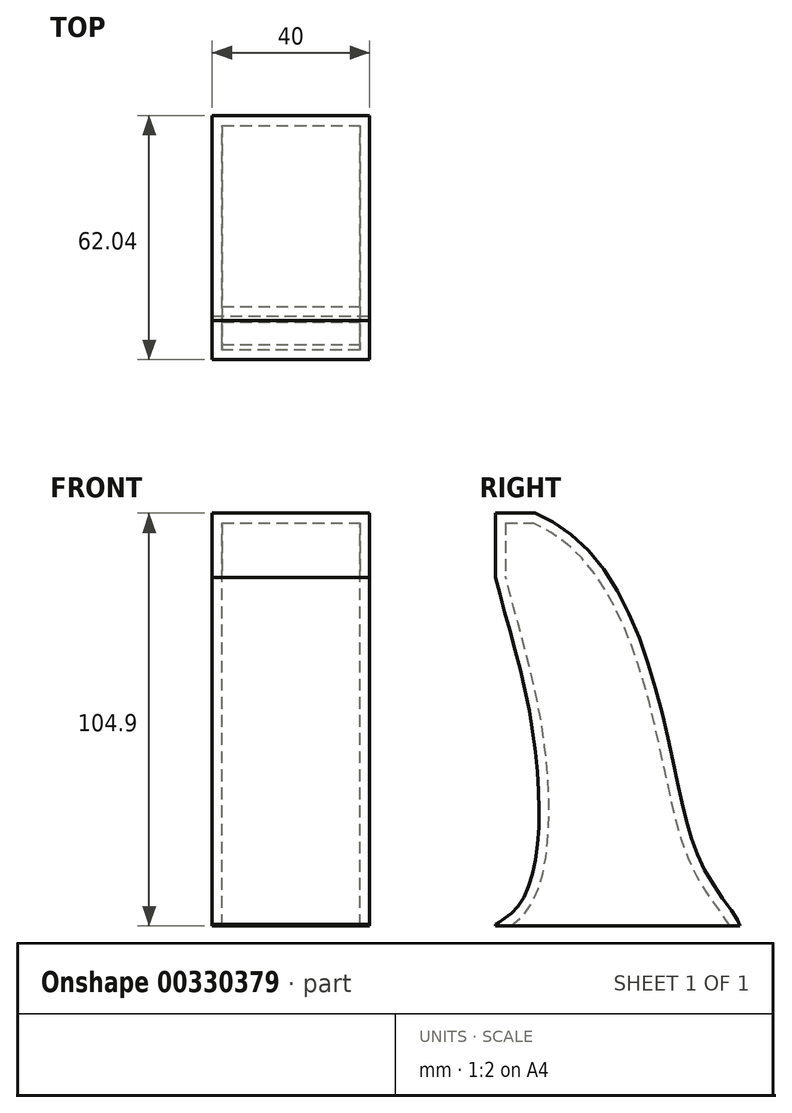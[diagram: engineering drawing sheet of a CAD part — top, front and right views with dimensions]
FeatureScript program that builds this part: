
annotation { "Feature Type Name" : "Feature", "Feature Type Description" : "" }
export const myFeature = defineFeature(function(context is Context, id is Id, definition is map)
    precondition{}
    {
        {
            var Q0;
            Q0=qCreatedBy(makeId("Right.planeOp"),FACE);
            var sketch = newSketch(context, id + "F0", { "sketchPlane" : qUnion([Q0])});
            skLineSegment(sketch, "E0.bottom", {"start": v(-44.84, 56) * mm, "end": v(43.69, 56) * mm});
            skLineSegment(sketch, "E0.top", {"start": v(-44.84, -48.91) * mm, "end": v(43.69, -48.91) * mm});
            skLineSegment(sketch, "E0.left", {"start": v(-44.84, 56) * mm, "end": v(-44.84, -48.91) * mm});
            skLineSegment(sketch, "E0.right", {"start": v(43.69, 56) * mm, "end": v(43.69, -48.91) * mm});
            skSolve(sketch);
        }
        {
            var Q0;
            Q0 = qSketchRegion(id + "F0", true);
            extrude(context, id + "F1", {"entities" : qUnion([Q0]), "depth" : 40 * mm});
        }
        {
            var Q0;
            Q0=makeQuery(id+"F1.opExtrude","CAP_FACE",FACE,{"disambiguationData":[OSD([sQuery(id+"F0.wireOp",EDGE,"E0.bottom"),sQuery(id+"F0.wireOp",EDGE,"E0.top"),sQuery(id+"F0.wireOp",EDGE,"E0.left"),sQuery(id+"F0.wireOp",EDGE,"E0.right")])],"isStart":false});
            var sketch = newSketch(context, id + "F2", { "sketchPlane" : qUnion([Q0])});
            skFitSpline(sketch, "E1", {"points": [v(-44.84, 56) * mm, v(-21.39, 46.55) * mm, v(0, -6.18) * mm, v(9.19, -36.38) * mm, v(17.2, -48.91) * mm, v(5.42, -48.91) * mm, v(-44.84, -48.91) * mm, v(-39.56, -44.37) * mm, v(-37, 9.15) * mm, v(-44.84, 56) * mm]});
            skSolve(sketch);
        }
        {
            var Q0;
            {var subQ5=makeQuery(id+"F1.opExtrude","CAP_EDGE",EDGE,{"disambiguationData":[OSD([sQuery(id+"F0.wireOp",EDGE,"E0.right")])],"isStart":false});Q0=makeQuery(id+"F2.imprint","IMPRINT",FACE,{"disambiguationData":[TD([[makeQuery(id+"F2.imprint","IMPRINT",EDGE,{"derivedFrom":subQ5}),-1.0]])]});}
            var Q1;
            {var subQ0=sQuery(id+"F2.wireOp",EDGE,"E1");var subQ1=makeQuery(id+"F1.opExtrude","CAP_EDGE",EDGE,{"disambiguationData":[OSD([sQuery(id+"F0.wireOp",EDGE,"E0.left")])],"isStart":false});var subQ2=makeQuery(id+"F2.imprint","INTERSECT",VERTEX,{"disambiguationData":[OD(0.0)],"derivedFrom":[subQ1,subQ0]});Q1=makeQuery(id+"F2.imprint","IMPRINT",FACE,{"disambiguationData":[TD([[makeQuery(id+"F2.imprint","IMPRINT",EDGE,{"disambiguationData":[TD([[subQ2,-1.0]])],"derivedFrom":subQ0}),1.0]])]});}
            extrude(context, id + "F3", {"entities" : qUnion([Q0, Q1]), "operationType" : NewBodyOperationType.REMOVE, "oppositeDirection" : true, "depth" : 40 * mm});
        }
        {
            var Q0;
            Q0=makeQuery(id+"F1.opExtrude","SWEPT_FACE",FACE,{"disambiguationData":[OSD([sQuery(id+"F0.wireOp",EDGE,"E0.top")])]});
            shell(context, id + "F4", {"entities" : qUnion([Q0]), "thickness" : 2.5 * mm});
        }
    });
